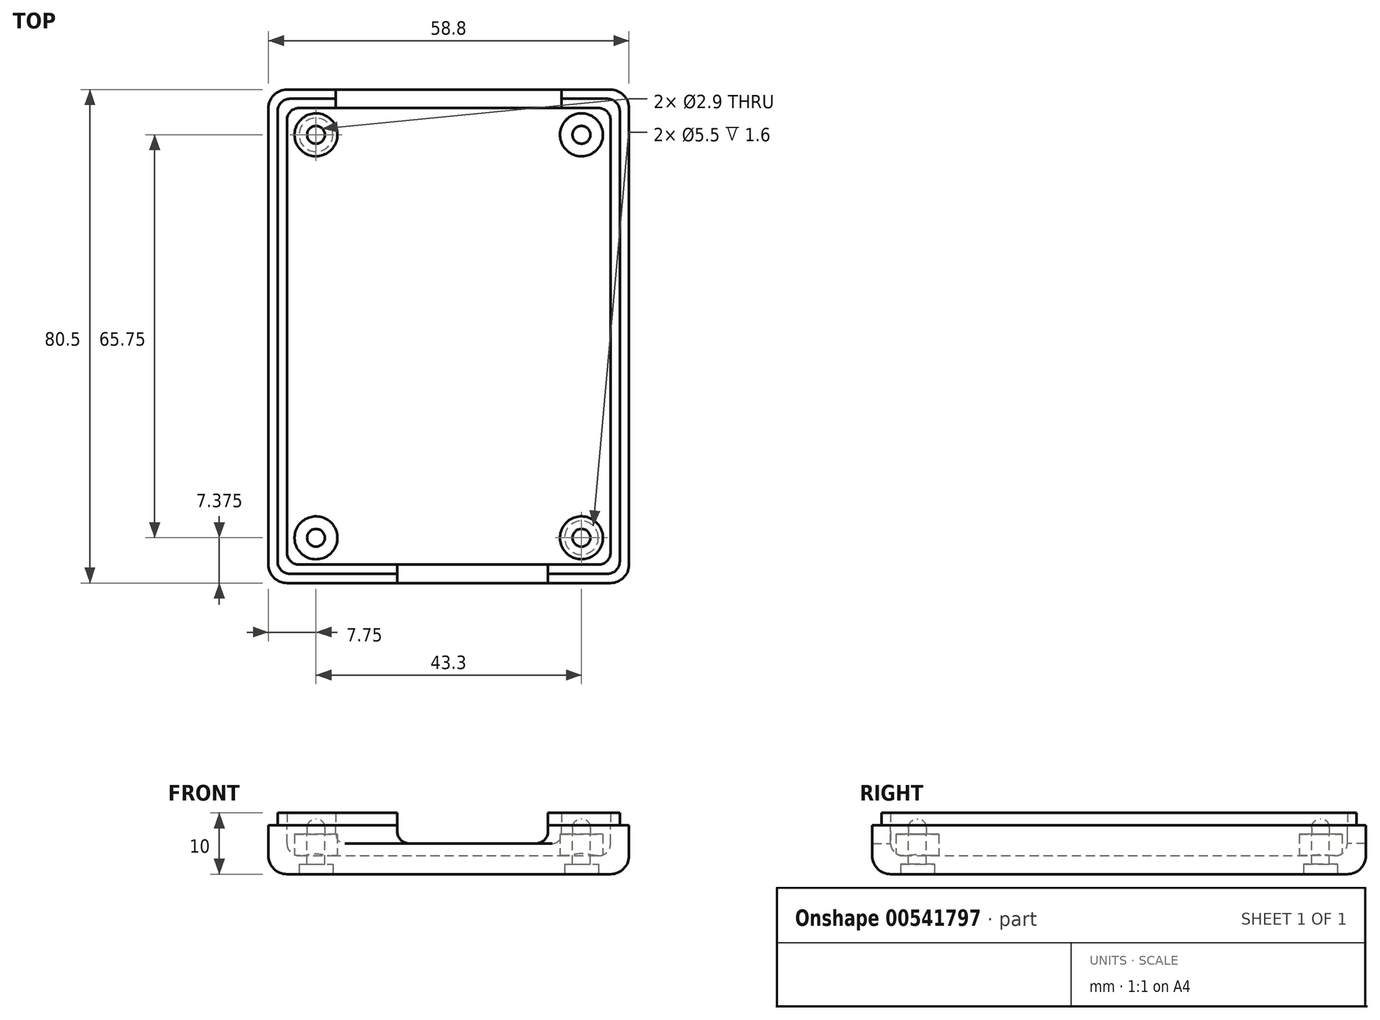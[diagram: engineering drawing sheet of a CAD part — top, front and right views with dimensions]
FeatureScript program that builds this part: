
annotation { "Feature Type Name" : "Feature", "Feature Type Description" : "" }
export const myFeature = defineFeature(function(context is Context, id is Id, definition is map)
    precondition{}
    {
        {
            var Q0;
            Q0=qCreatedBy(makeId("Top.planeOp"),FACE);
            var sketch = newSketch(context, id + "F0", { "sketchPlane" : qUnion([Q0])});
            skLineSegment(sketch, "E0.bottom", {"start": v(0, 0) * mm, "end": v(58.8, 0) * mm});
            skLineSegment(sketch, "E0.top", {"start": v(0, 80.5) * mm, "end": v(58.8, 80.5) * mm});
            skLineSegment(sketch, "E0.left", {"start": v(0, 0) * mm, "end": v(0, 80.5) * mm});
            skLineSegment(sketch, "E0.right", {"start": v(58.8, 0) * mm, "end": v(58.8, 80.5) * mm});
            skSolve(sketch);
        }
        {
            var Q0;
            Q0=makeQuery(id+"F0.imprint","IMPRINT",FACE,{"disambiguationData":[TD([[makeQuery(id+"F0.imprint","IMPRINT",EDGE,{"derivedFrom":sQuery(id+"F0.wireOp",EDGE,"E0.bottom")}),1.0]])]});
            extrude(context, id + "F1", {"entities" : qUnion([Q0]), "depth" : 8 * mm, "offsetDistance" : 25.4 * mm});
        }
        {
            var Q0;
            Q0=makeQuery(id+"F1.opExtrude","CAP_FACE",FACE,{"disambiguationData":[OSD([sQuery(id+"F0.wireOp",EDGE,"E0.bottom"),sQuery(id+"F0.wireOp",EDGE,"E0.top"),sQuery(id+"F0.wireOp",EDGE,"E0.left"),sQuery(id+"F0.wireOp",EDGE,"E0.right")])],"isStart":false});
            var sketch = newSketch(context, id + "F2", { "sketchPlane" : qUnion([Q0])});
            skLineSegment(sketch, "E1.bottom", {"start": v(3, 3) * mm, "end": v(55.8, 3) * mm});
            skLineSegment(sketch, "E1.top", {"start": v(3, 77.5) * mm, "end": v(55.8, 77.5) * mm});
            skLineSegment(sketch, "E1.left", {"start": v(3, 3) * mm, "end": v(3, 77.5) * mm});
            skLineSegment(sketch, "E1.right", {"start": v(55.8, 3) * mm, "end": v(55.8, 77.5) * mm});
            skSolve(sketch);
        }
        {
            var Q0;
            Q0=makeQuery(id+"F2.imprint","IMPRINT",FACE,{"disambiguationData":[TD([[makeQuery(id+"F2.imprint","IMPRINT",EDGE,{"derivedFrom":sQuery(id+"F2.wireOp",EDGE,"E1.bottom")}),1.0]])]});
            extrude(context, id + "F3", {"entities" : qUnion([Q0]), "operationType" : NewBodyOperationType.REMOVE, "oppositeDirection" : true, "depth" : 5 * mm, "offsetDistance" : 25.4 * mm});
        }
        {
            var Q0;
            Q0=makeQuery(id+"F3.boolean.opBoolean","COPY",FACE,{"derivedFrom":makeQuery(id+"F3.opExtrude","CAP_FACE",FACE,{"disambiguationData":[OSD([sQuery(id+"F2.wireOp",EDGE,"E1.bottom"),sQuery(id+"F2.wireOp",EDGE,"E1.top"),sQuery(id+"F2.wireOp",EDGE,"E1.left"),sQuery(id+"F2.wireOp",EDGE,"E1.right")])],"isStart":false})});
            var sketch = newSketch(context, id + "F4", { "sketchPlane" : qUnion([Q0])});
            skLineSegment(sketch, "E2.bottom", {"start": v(7.75, 7.38) * mm, "end": v(51.05, 7.38) * mm});
            skLineSegment(sketch, "E2.top", {"start": v(7.75, 73.13) * mm, "end": v(51.05, 73.13) * mm});
            skLineSegment(sketch, "E2.left", {"start": v(7.75, 7.38) * mm, "end": v(7.75, 73.13) * mm});
            skLineSegment(sketch, "E2.right", {"start": v(51.05, 7.38) * mm, "end": v(51.05, 73.13) * mm});
            skSolve(sketch);
        }
        {
            var Q0;
            Q0=makeQuery(id+"F4.imprint","IMPRINT",FACE,{"disambiguationData":[TD([[makeQuery(id+"F4.imprint","IMPRINT",EDGE,{"derivedFrom":sQuery(id+"F4.wireOp",EDGE,"E2.bottom")}),-1.0]])]});
            var sketch = newSketch(context, id + "F5", { "sketchPlane" : qUnion([Q0])});
            skCircle(sketch, "E3", {"center": v(7.75, 7.38) * mm, "radius": 3.5 * mm});
            skCircle(sketch, "E4", {"center": v(7.75, 73.13) * mm, "radius": 3.5 * mm});
            skCircle(sketch, "E5", {"center": v(51.05, 73.13) * mm, "radius": 3.5 * mm});
            skCircle(sketch, "E6", {"center": v(51.05, 7.38) * mm, "radius": 3.5 * mm});
            skSolve(sketch);
        }
        {
            var Q0;
            Q0 = qSketchRegion(id + "F5", true);
            extrude(context, id + "F6", {"entities" : qUnion([Q0]), "operationType" : NewBodyOperationType.ADD, "depth" : 3.5 * mm, "offsetDistance" : 25.4 * mm});
        }
        {
            var Q0;
            Q0=makeQuery(id+"F6.opExtrude","CAP_FACE",FACE,{"disambiguationData":[OSD([sQuery(id+"F5.wireOp",EDGE,"E6")])],"isStart":false});
            var sketch = newSketch(context, id + "F7", { "sketchPlane" : qUnion([Q0])});
            skCircle(sketch, "E7", {"center": v(51.05, 7.38) * mm, "radius": 1.45 * mm});
            skSolve(sketch);
        }
        {
            var Q0;
            Q0=makeQuery(id+"F6.opExtrude","CAP_FACE",FACE,{"disambiguationData":[OSD([sQuery(id+"F5.wireOp",EDGE,"E5")])],"isStart":false});
            var sketch = newSketch(context, id + "F8", { "sketchPlane" : qUnion([Q0])});
            skCircle(sketch, "E8", {"center": v(51.05, 73.13) * mm, "radius": 1.45 * mm});
            skSolve(sketch);
        }
        {
            var Q0;
            Q0=makeQuery(id+"F6.opExtrude","CAP_FACE",FACE,{"disambiguationData":[OSD([sQuery(id+"F5.wireOp",EDGE,"E4")])],"isStart":false});
            var sketch = newSketch(context, id + "F9", { "sketchPlane" : qUnion([Q0])});
            skCircle(sketch, "E9", {"center": v(7.75, 73.13) * mm, "radius": 1.45 * mm});
            skSolve(sketch);
        }
        {
            var Q0;
            Q0=makeQuery(id+"F6.opExtrude","CAP_FACE",FACE,{"disambiguationData":[OSD([sQuery(id+"F5.wireOp",EDGE,"E3")])],"isStart":false});
            var sketch = newSketch(context, id + "F10", { "sketchPlane" : qUnion([Q0])});
            skCircle(sketch, "E10", {"center": v(7.75, 7.38) * mm, "radius": 1.45 * mm});
            skSolve(sketch);
        }
        {
            var Q0;
            Q0 = qSketchRegion(id + "F9", true);
            var Q1;
            Q1 = qSketchRegion(id + "F7", true);
            extrude(context, id + "F11", {"entities" : qUnion([Q0, Q1]), "operationType" : NewBodyOperationType.REMOVE, "endBound" : BoundingType.THROUGH_ALL, "oppositeDirection" : true, "depth" : 2.5 * mm, "offsetDistance" : 25.4 * mm});
        }
        {
            var Q0;
            Q0 = qSketchRegion(id + "F8", true);
            var Q1;
            Q1 = qSketchRegion(id + "F10", true);
            var Q2;
            Q2 = qConstructionFilter(qBodyType(qCreatedBy(id + "F8" ,EDGE), BodyType.WIRE), ConstructionObject.NO);
            var Q3;
            Q3 = qConstructionFilter(qBodyType(qCreatedBy(id + "F10" ,EDGE), BodyType.WIRE), ConstructionObject.NO);
            extrude(context, id + "F12", {"entities" : qUnion([Q0, Q1]), "surfaceEntities" : qUnion([Q2, Q3]), "depth" : 2.5 * mm, "offsetDistance" : 25 * mm});
        }
        {
            var Q0;
            Q0=makeQuery(id+"F12.opExtrude","CAP_EDGE",EDGE,{"disambiguationData":[OSD([sQuery(id+"F10.wireOp",EDGE,"E10")])],"isStart":false});
            var Q1;
            Q1=makeQuery(id+"F12.opExtrude","CAP_EDGE",EDGE,{"disambiguationData":[OSD([sQuery(id+"F8.wireOp",EDGE,"E8")])],"isStart":false});
            fillet(context, id + "F13", {"entities" : qUnion([Q0, Q1]), "radius" : 1.4 * mm, "tangentPropagation" : true, "allowEdgeOverflow" : false});
        }
        {
            var Q0;
            Q0=makeQuery(id+"F1.opExtrude","CAP_FACE",FACE,{"disambiguationData":[OSD([sQuery(id+"F0.wireOp",EDGE,"E0.bottom"),sQuery(id+"F0.wireOp",EDGE,"E0.top"),sQuery(id+"F0.wireOp",EDGE,"E0.left"),sQuery(id+"F0.wireOp",EDGE,"E0.right")])],"isStart":false});
            var sketch = newSketch(context, id + "F14", { "sketchPlane" : qUnion([Q0])});
            skLineSegment(sketch, "E11.bottom", {"start": v(11, 80.5) * mm, "end": v(47.8, 80.5) * mm});
            skLineSegment(sketch, "E11.top", {"start": v(11, 77.5) * mm, "end": v(47.8, 77.5) * mm});
            skLineSegment(sketch, "E11.left", {"start": v(11, 80.5) * mm, "end": v(11, 77.5) * mm});
            skLineSegment(sketch, "E11.right", {"start": v(47.8, 80.5) * mm, "end": v(47.8, 77.5) * mm});
            skSolve(sketch);
        }
        {
            var Q0;
            Q0=makeQuery(id+"F14.imprint","IMPRINT",FACE,{"disambiguationData":[TD([[makeQuery(id+"F14.imprint","IMPRINT",EDGE,{"derivedFrom":sQuery(id+"F14.wireOp",EDGE,"E11.bottom")}),-1.0]])]});
            extrude(context, id + "F15", {"entities" : qUnion([Q0]), "operationType" : NewBodyOperationType.REMOVE, "oppositeDirection" : true, "depth" : 3 * mm, "offsetDistance" : 25.4 * mm});
        }
        {
            var Q0;
            Q0=makeQuery(id+"F1.opExtrude","CAP_FACE",FACE,{"disambiguationData":[OSD([sQuery(id+"F0.wireOp",EDGE,"E0.bottom"),sQuery(id+"F0.wireOp",EDGE,"E0.top"),sQuery(id+"F0.wireOp",EDGE,"E0.left"),sQuery(id+"F0.wireOp",EDGE,"E0.right")])],"isStart":false});
            var sketch = newSketch(context, id + "F16", { "sketchPlane" : qUnion([Q0])});
            skLineSegment(sketch, "E12.bottom", {"start": v(21, 0) * mm, "end": v(45.6, 0) * mm});
            skLineSegment(sketch, "E12.top", {"start": v(21, 3) * mm, "end": v(45.6, 3) * mm});
            skLineSegment(sketch, "E12.left", {"start": v(21, 0) * mm, "end": v(21, 3) * mm});
            skLineSegment(sketch, "E12.right", {"start": v(45.6, 0) * mm, "end": v(45.6, 3) * mm});
            skSolve(sketch);
        }
        {
            var Q0;
            Q0 = qSketchRegion(id + "F16", true);
            extrude(context, id + "F17", {"entities" : qUnion([Q0]), "operationType" : NewBodyOperationType.REMOVE, "oppositeDirection" : true, "depth" : 3 * mm, "offsetDistance" : 25.4 * mm});
        }
        {
            var Q0;
            {var subQ0=sQuery(id+"F0.wireOp",EDGE,"E0.right");var subQ1=sQuery(id+"F0.wireOp",EDGE,"E0.top");var subQ2=sQuery(id+"F0.wireOp",EDGE,"E0.bottom");Q0=makeQuery(id+"F17.boolean.opBoolean","SPLIT",FACE,{"disambiguationData":[TD([makeQuery(id+"F1.opExtrude","SWEPT_FACE",FACE,{"disambiguationData":[OSD([subQ0])]})])],"derivedFrom":makeQuery(id+"F1.opExtrude","CAP_FACE",FACE,{"disambiguationData":[OSD([subQ2,subQ1,sQuery(id+"F0.wireOp",EDGE,"E0.left"),subQ0])],"isStart":false})});}
            var sketch = newSketch(context, id + "F18", { "sketchPlane" : qUnion([Q0])});
            skLineSegment(sketch, "E13", {"start": v(45.6, 1.5) * mm, "end": v(58.8, 1.5) * mm, "construction": true});
            skLineSegment(sketch, "E14", {"start": v(47.8, 79) * mm, "end": v(58.8, 79) * mm, "construction": true});
            skLineSegment(sketch, "E15", {"start": v(58.8, 80.5) * mm, "end": v(55.8, 77.5) * mm, "construction": true});
            skLineSegment(sketch, "E16", {"start": v(55.8, 3) * mm, "end": v(58.8, 0) * mm, "construction": true});
            skLineSegment(sketch, "E17", {"start": v(47.8, 77.5) * mm, "end": v(47.8, 79) * mm});
            skLineSegment(sketch, "E18", {"start": v(57.3, 79) * mm, "end": v(57.3, 1.5) * mm});
            skLineSegment(sketch, "E19", {"start": v(57.3, 1.5) * mm, "end": v(45.6, 1.5) * mm});
            skLineSegment(sketch, "E20", {"start": v(45.6, 3) * mm, "end": v(55.8, 3) * mm});
            skLineSegment(sketch, "E21", {"start": v(55.8, 77.5) * mm, "end": v(47.8, 77.5) * mm});
            skLineSegment(sketch, "E22", {"start": v(47.8, 79) * mm, "end": v(57.3, 79) * mm});
            skLineSegment(sketch, "E23", {"start": v(55.8, 3) * mm, "end": v(55.8, 77.5) * mm});
            skLineSegment(sketch, "E24", {"start": v(45.6, 3) * mm, "end": v(45.6, 1.5) * mm});
            skSolve(sketch);
        }
        {
            var Q0;
            {var subQ0=sQuery(id+"F0.wireOp",EDGE,"E0.left");var subQ1=sQuery(id+"F0.wireOp",EDGE,"E0.top");var subQ2=sQuery(id+"F0.wireOp",EDGE,"E0.bottom");Q0=makeQuery(id+"F17.boolean.opBoolean","SPLIT",FACE,{"disambiguationData":[TD([makeQuery(id+"F1.opExtrude","SWEPT_FACE",FACE,{"disambiguationData":[OSD([subQ0])]})])],"derivedFrom":makeQuery(id+"F1.opExtrude","CAP_FACE",FACE,{"disambiguationData":[OSD([subQ2,subQ1,subQ0,sQuery(id+"F0.wireOp",EDGE,"E0.right")])],"isStart":false})});}
            var sketch = newSketch(context, id + "F19", { "sketchPlane" : qUnion([Q0])});
            skLineSegment(sketch, "E25", {"start": v(11, 79) * mm, "end": v(0, 79) * mm, "construction": true});
            skLineSegment(sketch, "E26", {"start": v(0, 79) * mm, "end": v(0, 80.5) * mm, "construction": true});
            skLineSegment(sketch, "E27", {"start": v(0, 80.5) * mm, "end": v(3, 77.5) * mm, "construction": true});
            skLineSegment(sketch, "E28", {"start": v(21, 1.5) * mm, "end": v(0, 1.5) * mm, "construction": true});
            skLineSegment(sketch, "E29", {"start": v(0, 1.5) * mm, "end": v(0, 0) * mm, "construction": true});
            skLineSegment(sketch, "E30", {"start": v(0, 0) * mm, "end": v(3, 3) * mm, "construction": true});
            skLineSegment(sketch, "E31", {"start": v(21, 1.5) * mm, "end": v(1.5, 1.5) * mm});
            skLineSegment(sketch, "E32", {"start": v(1.5, 1.5) * mm, "end": v(1.5, 79) * mm});
            skLineSegment(sketch, "E33", {"start": v(1.5, 79) * mm, "end": v(11, 79) * mm});
            skLineSegment(sketch, "E34", {"start": v(11, 77.5) * mm, "end": v(11, 79) * mm});
            skLineSegment(sketch, "E35", {"start": v(11, 77.5) * mm, "end": v(3, 77.5) * mm});
            skLineSegment(sketch, "E36", {"start": v(3, 77.5) * mm, "end": v(3, 3) * mm});
            skLineSegment(sketch, "E37", {"start": v(3, 3) * mm, "end": v(21, 3) * mm});
            skLineSegment(sketch, "E38", {"start": v(21, 3) * mm, "end": v(21, 1.5) * mm});
            skSolve(sketch);
        }
        {
            var Q0;
            Q0 = qSketchRegion(id + "F18", true);
            var Q1;
            Q1 = qSketchRegion(id + "F19", true);
            var Q2;
            Q2=sQuery(id+"F18.wireOp",EDGE,"E23");
            var Q3;
            Q3=sQuery(id+"F18.wireOp",EDGE,"E20");
            var Q4;
            Q4=sQuery(id+"F18.wireOp",EDGE,"E19");
            var Q5;
            Q5=sQuery(id+"F18.wireOp",EDGE,"E18");
            var Q6;
            Q6=sQuery(id+"F18.wireOp",EDGE,"E22");
            var Q7;
            Q7=sQuery(id+"F18.wireOp",EDGE,"E17");
            var Q8;
            Q8=sQuery(id+"F18.wireOp",EDGE,"E21");
            var Q9;
            Q9=sQuery(id+"F18.wireOp",EDGE,"E24");
            extrude(context, id + "F20", {"entities" : qUnion([Q0, Q1]), "surfaceEntities" : qUnion([Q2, Q3, Q4, Q5, Q6, Q7, Q8, Q9]), "depth" : 2 * mm, "offsetDistance" : 25 * mm});
        }
        {
            var Q0;
            Q0=makeQuery(id+"F1.opExtrude","SWEPT_EDGE",EDGE,{"disambiguationData":[OSD([sQuery(id+"F0.wireOp",EDGE,"E0.bottom"),sQuery(id+"F0.wireOp",EDGE,"E0.left")])]});
            var Q1;
            Q1=makeQuery(id+"F1.opExtrude","CAP_EDGE",EDGE,{"disambiguationData":[OSD([sQuery(id+"F0.wireOp",EDGE,"E0.bottom")])],"isStart":true});
            var Q2;
            Q2=makeQuery(id+"F1.opExtrude","SWEPT_EDGE",EDGE,{"disambiguationData":[OSD([sQuery(id+"F0.wireOp",EDGE,"E0.bottom"),sQuery(id+"F0.wireOp",EDGE,"E0.right")])]});
            var Q3;
            Q3=makeQuery(id+"F1.opExtrude","CAP_EDGE",EDGE,{"disambiguationData":[OSD([sQuery(id+"F0.wireOp",EDGE,"E0.left")])],"isStart":true});
            var Q4;
            Q4=makeQuery(id+"F1.opExtrude","SWEPT_EDGE",EDGE,{"disambiguationData":[OSD([sQuery(id+"F0.wireOp",EDGE,"E0.top"),sQuery(id+"F0.wireOp",EDGE,"E0.left")])]});
            var Q5;
            Q5=makeQuery(id+"F1.opExtrude","CAP_EDGE",EDGE,{"disambiguationData":[OSD([sQuery(id+"F0.wireOp",EDGE,"E0.top")])],"isStart":true});
            var Q6;
            Q6=makeQuery(id+"F1.opExtrude","SWEPT_EDGE",EDGE,{"disambiguationData":[OSD([sQuery(id+"F0.wireOp",EDGE,"E0.top"),sQuery(id+"F0.wireOp",EDGE,"E0.right")])]});
            var Q7;
            Q7=makeQuery(id+"F1.opExtrude","CAP_EDGE",EDGE,{"disambiguationData":[OSD([sQuery(id+"F0.wireOp",EDGE,"E0.right")])],"isStart":true});
            fillet(context, id + "F21", {"entities" : qUnion([Q0, Q1, Q2, Q3, Q4, Q5, Q6, Q7]), "radius" : 3 * mm, "tangentPropagation" : true, "allowEdgeOverflow" : false});
        }
        {
            var Q0;
            Q0=makeQuery(id+"F3.boolean.opBoolean","COPY",EDGE,{"derivedFrom":makeQuery(id+"F3.opExtrude","SWEPT_EDGE",EDGE,{"disambiguationData":[OSD([sQuery(id+"F2.wireOp",EDGE,"E1.bottom"),sQuery(id+"F2.wireOp",EDGE,"E1.right")])]})});
            var Q1;
            Q1=makeQuery(id+"F3.boolean.opBoolean","COPY",EDGE,{"derivedFrom":makeQuery(id+"F3.opExtrude","SWEPT_EDGE",EDGE,{"disambiguationData":[OSD([sQuery(id+"F2.wireOp",EDGE,"E1.bottom"),sQuery(id+"F2.wireOp",EDGE,"E1.left")])]})});
            var Q2;
            Q2=makeQuery(id+"F3.boolean.opBoolean","COPY",EDGE,{"derivedFrom":makeQuery(id+"F3.opExtrude","SWEPT_EDGE",EDGE,{"disambiguationData":[OSD([sQuery(id+"F2.wireOp",EDGE,"E1.top"),sQuery(id+"F2.wireOp",EDGE,"E1.left")])]})});
            var Q3;
            Q3=makeQuery(id+"F3.boolean.opBoolean","COPY",EDGE,{"derivedFrom":makeQuery(id+"F3.opExtrude","SWEPT_EDGE",EDGE,{"disambiguationData":[OSD([sQuery(id+"F2.wireOp",EDGE,"E1.top"),sQuery(id+"F2.wireOp",EDGE,"E1.right")])]})});
            var Q4;
            Q4=makeQuery(id+"F3.boolean.opBoolean","COPY",EDGE,{"derivedFrom":makeQuery(id+"F3.opExtrude","CAP_EDGE",EDGE,{"disambiguationData":[OSD([sQuery(id+"F2.wireOp",EDGE,"E1.right")])],"isStart":false})});
            var Q5;
            Q5=makeQuery(id+"F3.boolean.opBoolean","COPY",EDGE,{"derivedFrom":makeQuery(id+"F3.opExtrude","CAP_EDGE",EDGE,{"disambiguationData":[OSD([sQuery(id+"F2.wireOp",EDGE,"E1.bottom")])],"isStart":false})});
            var Q6;
            Q6=makeQuery(id+"F3.boolean.opBoolean","COPY",EDGE,{"derivedFrom":makeQuery(id+"F3.opExtrude","CAP_EDGE",EDGE,{"disambiguationData":[OSD([sQuery(id+"F2.wireOp",EDGE,"E1.left")])],"isStart":false})});
            var Q7;
            Q7=makeQuery(id+"F3.boolean.opBoolean","COPY",EDGE,{"derivedFrom":makeQuery(id+"F3.opExtrude","CAP_EDGE",EDGE,{"disambiguationData":[OSD([sQuery(id+"F2.wireOp",EDGE,"E1.top")])],"isStart":false})});
            var Q8;
            Q8=makeQuery(id+"F20.opExtrude","SWEPT_EDGE",EDGE,{"disambiguationData":[OSD([sQuery(id+"F18.wireOp",EDGE,"E20"),sQuery(id+"F18.wireOp",EDGE,"E23")])]});
            var Q9;
            Q9=makeQuery(id+"F20.opExtrude","SWEPT_EDGE",EDGE,{"disambiguationData":[OSD([sQuery(id+"F18.wireOp",EDGE,"E21"),sQuery(id+"F18.wireOp",EDGE,"E23")])]});
            var Q10;
            Q10=makeQuery(id+"F20.opExtrude","SWEPT_EDGE",EDGE,{"disambiguationData":[OSD([sQuery(id+"F19.wireOp",EDGE,"E36"),sQuery(id+"F19.wireOp",EDGE,"E37")])]});
            var Q11;
            Q11=makeQuery(id+"F20.opExtrude","SWEPT_EDGE",EDGE,{"disambiguationData":[OSD([sQuery(id+"F19.wireOp",EDGE,"E35"),sQuery(id+"F19.wireOp",EDGE,"E36")])]});
            fillet(context, id + "F22", {"entities" : qUnion([Q0, Q1, Q2, Q3, Q4, Q5, Q6, Q7, Q8, Q9, Q10, Q11]), "radius" : 2 * mm, "tangentPropagation" : true, "allowEdgeOverflow" : false});
        }
        {
            var Q0;
            Q0=makeQuery(id+"F20.opExtrude","SWEPT_EDGE",EDGE,{"disambiguationData":[OSD([sQuery(id+"F18.wireOp",EDGE,"E18"),sQuery(id+"F18.wireOp",EDGE,"E22")])]});
            var Q1;
            Q1=makeQuery(id+"F20.opExtrude","SWEPT_EDGE",EDGE,{"disambiguationData":[OSD([sQuery(id+"F19.wireOp",EDGE,"E32"),sQuery(id+"F19.wireOp",EDGE,"E33")])]});
            var Q2;
            Q2=makeQuery(id+"F20.opExtrude","SWEPT_EDGE",EDGE,{"disambiguationData":[OSD([sQuery(id+"F19.wireOp",EDGE,"E31"),sQuery(id+"F19.wireOp",EDGE,"E32")])]});
            var Q3;
            Q3=makeQuery(id+"F20.opExtrude","SWEPT_EDGE",EDGE,{"disambiguationData":[OSD([sQuery(id+"F18.wireOp",EDGE,"E18"),sQuery(id+"F18.wireOp",EDGE,"E19")])]});
            fillet(context, id + "F23", {"entities" : qUnion([Q0, Q1, Q2, Q3]), "radius" : 2 * mm, "tangentPropagation" : true, "allowEdgeOverflow" : false});
        }
        {
            var Q0;
            Q0=makeQuery(id+"F15.boolean.opBoolean","COPY",EDGE,{"derivedFrom":makeQuery(id+"F15.opExtrude","CAP_EDGE",EDGE,{"disambiguationData":[OSD([sQuery(id+"F14.wireOp",EDGE,"E11.left")])],"isStart":false})});
            var Q1;
            Q1=makeQuery(id+"F15.boolean.opBoolean","COPY",EDGE,{"derivedFrom":makeQuery(id+"F15.opExtrude","CAP_EDGE",EDGE,{"disambiguationData":[OSD([sQuery(id+"F14.wireOp",EDGE,"E11.right")])],"isStart":false})});
            fillet(context, id + "F24", {"entities" : qUnion([Q0, Q1]), "radius" : 1.5 * mm, "tangentPropagation" : true, "allowEdgeOverflow" : false});
        }
        {
            var Q0;
            Q0=makeQuery(id+"F17.boolean.opBoolean","COPY",EDGE,{"derivedFrom":makeQuery(id+"F17.opExtrude","CAP_EDGE",EDGE,{"disambiguationData":[OSD([sQuery(id+"F16.wireOp",EDGE,"E12.left")])],"isStart":false})});
            var Q1;
            Q1=makeQuery(id+"F17.boolean.opBoolean","COPY",EDGE,{"derivedFrom":makeQuery(id+"F17.opExtrude","CAP_EDGE",EDGE,{"disambiguationData":[OSD([sQuery(id+"F16.wireOp",EDGE,"E12.right")])],"isStart":false})});
            fillet(context, id + "F25", {"entities" : qUnion([Q0, Q1]), "radius" : 2 * mm, "tangentPropagation" : true, "allowEdgeOverflow" : false});
        }
        {
            var Q0;
            Q0=makeQuery(id+"F1.opExtrude","CAP_FACE",FACE,{"disambiguationData":[OSD([sQuery(id+"F0.wireOp",EDGE,"E0.bottom"),sQuery(id+"F0.wireOp",EDGE,"E0.top"),sQuery(id+"F0.wireOp",EDGE,"E0.left"),sQuery(id+"F0.wireOp",EDGE,"E0.right")])],"isStart":true});
            var sketch = newSketch(context, id + "F26", { "sketchPlane" : qUnion([Q0])});
            skCircle(sketch, "E39", {"center": v(51.05, -7.38) * mm, "radius": 2.75 * mm});
            skCircle(sketch, "E40", {"center": v(7.75, -73.13) * mm, "radius": 2.75 * mm});
            skSolve(sketch);
        }
        {
            var Q0;
            Q0 = qSketchRegion(id + "F26", true);
            extrude(context, id + "F27", {"entities" : qUnion([Q0]), "operationType" : NewBodyOperationType.REMOVE, "oppositeDirection" : true, "depth" : 1.6 * mm, "offsetDistance" : 25 * mm});
        }
    });
